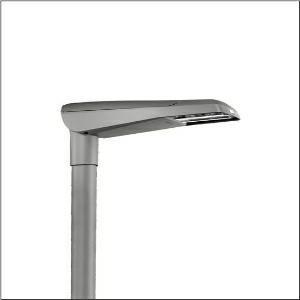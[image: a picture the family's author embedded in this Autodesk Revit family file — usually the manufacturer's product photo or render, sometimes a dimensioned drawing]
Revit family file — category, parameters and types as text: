
# Revit family: streetlight_sl_11_iq_micro___p1_0a_5xc1c51f08ce_61b4
name_source: partatom
category: Lighting Fixtures
units: mm (PartAtom-declared; Revit-internal decimal feet)

## family parameters
Cut with Voids When Loaded = No
Host = Face
Light Source = No
Part Type = Normal
Room Calculation Point = No
Round Connector Dimension = Use Diameter
Shared = No

## types (1)
- --- (1 x LED, 1600 lm, 10.8 W, 3000K)
    Apparent Load = 11 VA
    CIE Flux Codes = 29 63 93 100 100
    Color Rendering = 70
    Color Temperature = 3000K
    Default Elevation = 1800 mm
    Description = Streetlight SL 11 iQ micro, mast luminaire, primary light control with 3 zone facetted reflector, of plastic, silver coated, highly specular, primary optical cover: cover, of PMMA, transparent, light distribution: P1.0a, light emission: direct distribution, primary light characteristic: asymmetric, installation type: post-top, side-entry, lamps: LED, High Power LED, rated values: 1.600lm | 10,8W | 148,1lm/W (begin service life); end service life: 1.600lm | 11,1W; at 50% lumin. flux: 800lm | 6W | 133,3lm/W, colour temperature: 3000K, colour rendering: CRI > 70, light colour: 730, light setting 1 begin service life: 100% | 1.600lm | 10,8W | 148,1lm/W | 3.000K, light setting 1 end service life: 11,1W, further light settings possible, control: Street-Remote, optimised constant luminous flux control (CLO 2.0), Desk-Remote (wireless, voltage-free reading and setting of iQ features in the workshop via application-optimized NFC function/RFID function), Light-Fading, Smart-Wire, Night-Set, Lumen-Switch, Temp-Guard, Auto-Match, with cable H07RN-F 5x 1.5mm², mains connection: 230..240V, AC, 50/60Hz, connection cable pre-assembled, cable length: 5,5m, luminaire housing, of diecast aluminium, powder-coated, Siteco® metallic grey (DB 702S), please order mast flange separately, inclination adjustable without tools: 0°, 5°, 10°, 15° (post-top) | 0°, -5°, -10°, -15° (side-entry), sealing non-destructively replaceable, multi-level sealing system, length: 600mm, width: 174mm, height: 116mm, mast flange for spigot size: 42mm (side-entry): 5XC10008XM4, 60/48mm (side-entry/post-top): 5XC10108XM2, 76/60mm (side-entry/post-top): 5XC10108XM1, equipment: standard, protection rating (complete): IP66, insulation class (complete): insulation class II (safety insulation), certification: CE, ENEC, ENEC+, VDE, impact resistance: IK10, permissible operating ambient temperature for outdoor applications: -25..+50°C, standard-compliant lighting for roads and squares, Environmental Product Declaration (EPD) tested and certified by an independent institute, packaging unit: 1 piece

Light Distribution: P1.0a
    Height = 116 mm
    Lamp = 1 x LED
    Lamp Light Flux = 1600 lm
    Lamp Power = 10.8 W
    Lamp count = 1
    Length = 600 mm
    Luminous efficacy = 148 lm/W
    Manufacturer = Siteco
    ModVariant = No
    Model = 5XC1C51F08CE
    Number of Poles = 1
    OnlyDefault = Yes
    Power Factor = 1
    Product Name = Streetlight SL 11 iQ micro | P1.0a
    Product group = mast luminaire | pylon top
    ProductGroupID = 6100
    Protection Class = Protection class II
    Protection Degree = IP 66
    RLX_Detail_Level = 1
    RLX_Emergency_Light_Flux = 0 lm
    RLX_Emergency_Type = 0
    RLX_Emergency_Type_DB = No
    RlxData = <blob elided: 26641 chars, md5=dc6ef0c1>
    Socket = socket
    Standby Power = 0 W
    System Light Flux = 1600 lm
    System Power = 11 W
    Type Comments = factory setting: luminous flux: 100 % | dim-lin: 254 | 194 mA
    Type Image = l_1006566.jpg
    URL = http://relux.com
    VarID = @adj_018149
    Voltage = 0 V
    Weight = 0.00 kg
    Width = 174 mm

## geometry (parser evidence)
native form markers: Blend x4, Sweep x11
no freeform markers — native parametric forms only
